# Revit family: BuzziWrap Desk
name_source: partatom
category: Furniture
revit_build: Autodesk Revit 2015 (Build: 20141119_0715(x64)
units: mm (PartAtom-declared; Revit-internal decimal feet)

## types (17) — shared parameters
BuzziWrap Desk Right Terminate 20.67x 26.18 = No
Middle Panel Length = 3' - 0"
Panel Material = <By Category>

## per-type parameters (varying)
- BuzziWrap Desk Full- 28.54 x 26.18: BuzziWrap Desk Center 20.67x 18.31=No; BuzziWrap Desk Center 20.67x 26.18=No; BuzziWrap Desk Center 24.61x 18.31=No; BuzziWrap Desk Center 24.61x 26.18=No; BuzziWrap Desk Center 28.54x 18.31=No; BuzziWrap Desk Center 28.54x 26.18=Yes; BuzziWrap Desk Left 20.67x 18.31=No; BuzziWrap Desk Left 20.67x 26.18=No; BuzziWrap Desk Left 24.61x 18.31=No; BuzziWrap Desk Left 24.61x 26.18=No; BuzziWrap Desk Left 28.54x 18.31=No; BuzziWrap Desk Left 28.54x 26.18=No; BuzziWrap Desk Left Terminate 20.67x 18.31=No; BuzziWrap Desk Left Terminate 20.67x 26.18=No; BuzziWrap Desk Left Terminate 24.61x 18.31=No; BuzziWrap Desk Left Terminate 24.61x 26.18=No; BuzziWrap Desk Left Terminate 28.54x 18.31=No; BuzziWrap Desk Left Terminate 28.54x 26.18=Yes; BuzziWrap Desk Right 20.67x 18.31=No; BuzziWrap Desk Right 20.67x 26.18=No; BuzziWrap Desk Right 24.61x 18.31=No; BuzziWrap Desk Right 24.61x 26.18=No; BuzziWrap Desk Right 28.54x 18.31=No; BuzziWrap Desk Right 28.54x 26.18=Yes; BuzziWrap Desk Right Terminate 20.67x 18.31=No; BuzziWrap Desk Right Terminate 24.61x 18.31=No; BuzziWrap Desk Right Terminate 24.61x 26.18=No; BuzziWrap Desk Right Terminate 28.54x 18.31=No; BuzziWrap Desk Right Terminate 28.54x 26.18=No
- BuzziWrap Desk Left- 28.54 x 26.18: BuzziWrap Desk Center 20.67x 18.31=No; BuzziWrap Desk Center 20.67x 26.18=No; BuzziWrap Desk Center 24.61x 18.31=No; BuzziWrap Desk Center 24.61x 26.18=No; BuzziWrap Desk Center 28.54x 18.31=No; BuzziWrap Desk Center 28.54x 26.18=Yes; BuzziWrap Desk Left 20.67x 18.31=No; BuzziWrap Desk Left 20.67x 26.18=No; BuzziWrap Desk Left 24.61x 18.31=No; BuzziWrap Desk Left 24.61x 26.18=No; BuzziWrap Desk Left 28.54x 18.31=No; BuzziWrap Desk Left 28.54x 26.18=Yes; BuzziWrap Desk Left Terminate 20.67x 18.31=No; BuzziWrap Desk Left Terminate 20.67x 26.18=No; BuzziWrap Desk Left Terminate 24.61x 18.31=No; BuzziWrap Desk Left Terminate 24.61x 26.18=No; BuzziWrap Desk Left Terminate 28.54x 18.31=No; BuzziWrap Desk Left Terminate 28.54x 26.18=No; BuzziWrap Desk Right 20.67x 18.31=No; BuzziWrap Desk Right 20.67x 26.18=No; BuzziWrap Desk Right 24.61x 18.31=No; BuzziWrap Desk Right 24.61x 26.18=No; BuzziWrap Desk Right 28.54x 18.31=No; BuzziWrap Desk Right 28.54x 26.18=No; BuzziWrap Desk Right Terminate 20.67x 18.31=No; BuzziWrap Desk Right Terminate 24.61x 18.31=No; BuzziWrap Desk Right Terminate 24.61x 26.18=No; BuzziWrap Desk Right Terminate 28.54x 18.31=No; BuzziWrap Desk Right Terminate 28.54x 26.18=Yes
- BuzziWrap Desk Right- 28.54 x 26.18: BuzziWrap Desk Center 20.67x 18.31=No; BuzziWrap Desk Center 20.67x 26.18=No; BuzziWrap Desk Center 24.61x 18.31=No; BuzziWrap Desk Center 24.61x 26.18=No; BuzziWrap Desk Center 28.54x 18.31=No; BuzziWrap Desk Center 28.54x 26.18=Yes; BuzziWrap Desk Left 20.67x 18.31=No; BuzziWrap Desk Left 20.67x 26.18=No; BuzziWrap Desk Left 24.61x 18.31=No; BuzziWrap Desk Left 24.61x 26.18=No; BuzziWrap Desk Left 28.54x 18.31=No; BuzziWrap Desk Left 28.54x 26.18=No; BuzziWrap Desk Left Terminate 20.67x 18.31=No; BuzziWrap Desk Left Terminate 20.67x 26.18=No; BuzziWrap Desk Left Terminate 24.61x 18.31=No; BuzziWrap Desk Left Terminate 24.61x 26.18=No; BuzziWrap Desk Left Terminate 28.54x 18.31=No; BuzziWrap Desk Left Terminate 28.54x 26.18=Yes; BuzziWrap Desk Right 20.67x 18.31=No; BuzziWrap Desk Right 20.67x 26.18=No; BuzziWrap Desk Right 24.61x 18.31=No; BuzziWrap Desk Right 24.61x 26.18=No; BuzziWrap Desk Right 28.54x 18.31=No; BuzziWrap Desk Right 28.54x 26.18=Yes; BuzziWrap Desk Right Terminate 20.67x 18.31=No; BuzziWrap Desk Right Terminate 24.61x 18.31=No; BuzziWrap Desk Right Terminate 24.61x 26.18=No; BuzziWrap Desk Right Terminate 28.54x 18.31=No; BuzziWrap Desk Right Terminate 28.54x 26.18=No
- BuzziWrap Desk Full- 28.54 x 18.31: BuzziWrap Desk Center 20.67x 18.31=No; BuzziWrap Desk Center 20.67x 26.18=No; BuzziWrap Desk Center 24.61x 18.31=No; BuzziWrap Desk Center 24.61x 26.18=No; BuzziWrap Desk Center 28.54x 18.31=Yes; BuzziWrap Desk Center 28.54x 26.18=No; BuzziWrap Desk Left 20.67x 18.31=No; BuzziWrap Desk Left 20.67x 26.18=No; BuzziWrap Desk Left 24.61x 18.31=No; BuzziWrap Desk Left 24.61x 26.18=No; BuzziWrap Desk Left 28.54x 18.31=Yes; BuzziWrap Desk Left 28.54x 26.18=No; BuzziWrap Desk Left Terminate 20.67x 18.31=No; BuzziWrap Desk Left Terminate 20.67x 26.18=No; BuzziWrap Desk Left Terminate 24.61x 18.31=No; BuzziWrap Desk Left Terminate 24.61x 26.18=No; BuzziWrap Desk Left Terminate 28.54x 18.31=No; BuzziWrap Desk Left Terminate 28.54x 26.18=No; BuzziWrap Desk Right 20.67x 18.31=No; BuzziWrap Desk Right 20.67x 26.18=No; BuzziWrap Desk Right 24.61x 18.31=No; BuzziWrap Desk Right 24.61x 26.18=No; BuzziWrap Desk Right 28.54x 18.31=Yes; BuzziWrap Desk Right 28.54x 26.18=No; BuzziWrap Desk Right Terminate 20.67x 18.31=No; BuzziWrap Desk Right Terminate 24.61x 18.31=No; BuzziWrap Desk Right Terminate 24.61x 26.18=No; BuzziWrap Desk Right Terminate 28.54x 18.31=No; BuzziWrap Desk Right Terminate 28.54x 26.18=No
- BuzziWrap Desk Left- 28.54 x 18.31: BuzziWrap Desk Center 20.67x 18.31=No; BuzziWrap Desk Center 20.67x 26.18=No; BuzziWrap Desk Center 24.61x 18.31=No; BuzziWrap Desk Center 24.61x 26.18=No; BuzziWrap Desk Center 28.54x 18.31=Yes; BuzziWrap Desk Center 28.54x 26.18=No; BuzziWrap Desk Left 20.67x 18.31=No; BuzziWrap Desk Left 20.67x 26.18=No; BuzziWrap Desk Left 24.61x 18.31=No; BuzziWrap Desk Left 24.61x 26.18=No; BuzziWrap Desk Left 28.54x 18.31=Yes; BuzziWrap Desk Left 28.54x 26.18=No; BuzziWrap Desk Left Terminate 20.67x 18.31=No; BuzziWrap Desk Left Terminate 20.67x 26.18=No; BuzziWrap Desk Left Terminate 24.61x 18.31=No; BuzziWrap Desk Left Terminate 24.61x 26.18=No; BuzziWrap Desk Left Terminate 28.54x 18.31=No; BuzziWrap Desk Left Terminate 28.54x 26.18=No; BuzziWrap Desk Right 20.67x 18.31=No; BuzziWrap Desk Right 20.67x 26.18=No; BuzziWrap Desk Right 24.61x 18.31=No; BuzziWrap Desk Right 24.61x 26.18=No; BuzziWrap Desk Right 28.54x 18.31=No; BuzziWrap Desk Right 28.54x 26.18=No; BuzziWrap Desk Right Terminate 20.67x 18.31=No; BuzziWrap Desk Right Terminate 24.61x 18.31=No; BuzziWrap Desk Right Terminate 24.61x 26.18=No; BuzziWrap Desk Right Terminate 28.54x 18.31=Yes; BuzziWrap Desk Right Terminate 28.54x 26.18=No
- BuzziWrap Desk Right- 28.54 x 18.31: BuzziWrap Desk Center 20.67x 18.31=No; BuzziWrap Desk Center 20.67x 26.18=No; BuzziWrap Desk Center 24.61x 18.31=No; BuzziWrap Desk Center 24.61x 26.18=No; BuzziWrap Desk Center 28.54x 18.31=Yes; BuzziWrap Desk Center 28.54x 26.18=No; BuzziWrap Desk Left 20.67x 18.31=No; BuzziWrap Desk Left 20.67x 26.18=No; BuzziWrap Desk Left 24.61x 18.31=No; BuzziWrap Desk Left 24.61x 26.18=No; BuzziWrap Desk Left 28.54x 18.31=No; BuzziWrap Desk Left 28.54x 26.18=No; BuzziWrap Desk Left Terminate 20.67x 18.31=No; BuzziWrap Desk Left Terminate 20.67x 26.18=No; BuzziWrap Desk Left Terminate 24.61x 18.31=No; BuzziWrap Desk Left Terminate 24.61x 26.18=No; BuzziWrap Desk Left Terminate 28.54x 18.31=Yes; BuzziWrap Desk Left Terminate 28.54x 26.18=No; BuzziWrap Desk Right 20.67x 18.31=No; BuzziWrap Desk Right 20.67x 26.18=No; BuzziWrap Desk Right 24.61x 18.31=No; BuzziWrap Desk Right 24.61x 26.18=No; BuzziWrap Desk Right 28.54x 18.31=Yes; BuzziWrap Desk Right 28.54x 26.18=No; BuzziWrap Desk Right Terminate 20.67x 18.31=No; BuzziWrap Desk Right Terminate 24.61x 18.31=No; BuzziWrap Desk Right Terminate 24.61x 26.18=No; BuzziWrap Desk Right Terminate 28.54x 18.31=No; BuzziWrap Desk Right Terminate 28.54x 26.18=No
- BuzziWrap desk Full- 24.61 x 26.18: BuzziWrap Desk Center 20.67x 18.31=No; BuzziWrap Desk Center 20.67x 26.18=No; BuzziWrap Desk Center 24.61x 18.31=No; BuzziWrap Desk Center 24.61x 26.18=Yes; BuzziWrap Desk Center 28.54x 18.31=No; BuzziWrap Desk Center 28.54x 26.18=No; BuzziWrap Desk Left 20.67x 18.31=No; BuzziWrap Desk Left 20.67x 26.18=No; BuzziWrap Desk Left 24.61x 18.31=No; BuzziWrap Desk Left 24.61x 26.18=Yes; BuzziWrap Desk Left 28.54x 18.31=No; BuzziWrap Desk Left 28.54x 26.18=No; BuzziWrap Desk Left Terminate 20.67x 18.31=No; BuzziWrap Desk Left Terminate 20.67x 26.18=No; BuzziWrap Desk Left Terminate 24.61x 18.31=No; BuzziWrap Desk Left Terminate 24.61x 26.18=No; BuzziWrap Desk Left Terminate 28.54x 18.31=No; BuzziWrap Desk Left Terminate 28.54x 26.18=No; BuzziWrap Desk Right 20.67x 18.31=No; BuzziWrap Desk Right 20.67x 26.18=No; BuzziWrap Desk Right 24.61x 18.31=No; BuzziWrap Desk Right 24.61x 26.18=Yes; BuzziWrap Desk Right 28.54x 18.31=No; BuzziWrap Desk Right 28.54x 26.18=No; BuzziWrap Desk Right Terminate 20.67x 18.31=No; BuzziWrap Desk Right Terminate 24.61x 18.31=No; BuzziWrap Desk Right Terminate 24.61x 26.18=No; BuzziWrap Desk Right Terminate 28.54x 18.31=No; BuzziWrap Desk Right Terminate 28.54x 26.18=No
- BuzziWrap desk Left- 24.61 x 26.18: BuzziWrap Desk Center 20.67x 18.31=No; BuzziWrap Desk Center 20.67x 26.18=No; BuzziWrap Desk Center 24.61x 18.31=Yes; BuzziWrap Desk Center 24.61x 26.18=Yes; BuzziWrap Desk Center 28.54x 18.31=No; BuzziWrap Desk Center 28.54x 26.18=No; BuzziWrap Desk Left 20.67x 18.31=No; BuzziWrap Desk Left 20.67x 26.18=No; BuzziWrap Desk Left 24.61x 18.31=No; BuzziWrap Desk Left 24.61x 26.18=Yes; BuzziWrap Desk Left 28.54x 18.31=No; BuzziWrap Desk Left 28.54x 26.18=No; BuzziWrap Desk Left Terminate 20.67x 18.31=Yes; BuzziWrap Desk Left Terminate 20.67x 26.18=No; BuzziWrap Desk Left Terminate 24.61x 18.31=Yes; BuzziWrap Desk Left Terminate 24.61x 26.18=No; BuzziWrap Desk Left Terminate 28.54x 18.31=No; BuzziWrap Desk Left Terminate 28.54x 26.18=No; BuzziWrap Desk Right 20.67x 18.31=No; BuzziWrap Desk Right 20.67x 26.18=No; BuzziWrap Desk Right 24.61x 18.31=No; BuzziWrap Desk Right 24.61x 26.18=No; BuzziWrap Desk Right 28.54x 18.31=No; BuzziWrap Desk Right 28.54x 26.18=No; BuzziWrap Desk Right Terminate 20.67x 18.31=Yes; BuzziWrap Desk Right Terminate 24.61x 18.31=Yes; BuzziWrap Desk Right Terminate 24.61x 26.18=Yes; BuzziWrap Desk Right Terminate 28.54x 18.31=No; BuzziWrap Desk Right Terminate 28.54x 26.18=No
- BuzziWrap Desk Right 24.61 x 26.18: BuzziWrap Desk Center 20.67x 18.31=No; BuzziWrap Desk Center 20.67x 26.18=No; BuzziWrap Desk Center 24.61x 18.31=No; BuzziWrap Desk Center 24.61x 26.18=Yes; BuzziWrap Desk Center 28.54x 18.31=No; BuzziWrap Desk Center 28.54x 26.18=No; BuzziWrap Desk Left 20.67x 18.31=No; BuzziWrap Desk Left 20.67x 26.18=No; BuzziWrap Desk Left 24.61x 18.31=No; BuzziWrap Desk Left 24.61x 26.18=No; BuzziWrap Desk Left 28.54x 18.31=No; BuzziWrap Desk Left 28.54x 26.18=No; BuzziWrap Desk Left Terminate 20.67x 18.31=No; BuzziWrap Desk Left Terminate 20.67x 26.18=No; BuzziWrap Desk Left Terminate 24.61x 18.31=No; BuzziWrap Desk Left Terminate 24.61x 26.18=Yes; BuzziWrap Desk Left Terminate 28.54x 18.31=No; BuzziWrap Desk Left Terminate 28.54x 26.18=No; BuzziWrap Desk Right 20.67x 18.31=No; BuzziWrap Desk Right 20.67x 26.18=No; BuzziWrap Desk Right 24.61x 18.31=No; BuzziWrap Desk Right 24.61x 26.18=Yes; BuzziWrap Desk Right 28.54x 18.31=No; BuzziWrap Desk Right 28.54x 26.18=No; BuzziWrap Desk Right Terminate 20.67x 18.31=No; BuzziWrap Desk Right Terminate 24.61x 18.31=No; BuzziWrap Desk Right Terminate 24.61x 26.18=No; BuzziWrap Desk Right Terminate 28.54x 18.31=No; BuzziWrap Desk Right Terminate 28.54x 26.18=No
- BuzziWrap Desk Full 24.61 x 18.31: BuzziWrap Desk Center 20.67x 18.31=No; BuzziWrap Desk Center 20.67x 26.18=No; BuzziWrap Desk Center 24.61x 18.31=Yes; BuzziWrap Desk Center 24.61x 26.18=No; BuzziWrap Desk Center 28.54x 18.31=No; BuzziWrap Desk Center 28.54x 26.18=No; BuzziWrap Desk Left 20.67x 18.31=No; BuzziWrap Desk Left 20.67x 26.18=No; BuzziWrap Desk Left 24.61x 18.31=Yes; BuzziWrap Desk Left 24.61x 26.18=No; BuzziWrap Desk Left 28.54x 18.31=No; BuzziWrap Desk Left 28.54x 26.18=No; BuzziWrap Desk Left Terminate 20.67x 18.31=No; BuzziWrap Desk Left Terminate 20.67x 26.18=No; BuzziWrap Desk Left Terminate 24.61x 18.31=No; BuzziWrap Desk Left Terminate 24.61x 26.18=No; BuzziWrap Desk Left Terminate 28.54x 18.31=No; BuzziWrap Desk Left Terminate 28.54x 26.18=No; BuzziWrap Desk Right 20.67x 18.31=No; BuzziWrap Desk Right 20.67x 26.18=No; BuzziWrap Desk Right 24.61x 18.31=Yes; BuzziWrap Desk Right 24.61x 26.18=No; BuzziWrap Desk Right 28.54x 18.31=No; BuzziWrap Desk Right 28.54x 26.18=No; BuzziWrap Desk Right Terminate 20.67x 18.31=No; BuzziWrap Desk Right Terminate 24.61x 18.31=No; BuzziWrap Desk Right Terminate 24.61x 26.18=No; BuzziWrap Desk Right Terminate 28.54x 18.31=No; BuzziWrap Desk Right Terminate 28.54x 26.18=No
- BuzziWrap Desk Left 24.61 x 18.31: BuzziWrap Desk Center 20.67x 18.31=No; BuzziWrap Desk Center 20.67x 26.18=No; BuzziWrap Desk Center 24.61x 18.31=Yes; BuzziWrap Desk Center 24.61x 26.18=No; BuzziWrap Desk Center 28.54x 18.31=No; BuzziWrap Desk Center 28.54x 26.18=No; BuzziWrap Desk Left 20.67x 18.31=No; BuzziWrap Desk Left 20.67x 26.18=No; BuzziWrap Desk Left 24.61x 18.31=Yes; BuzziWrap Desk Left 24.61x 26.18=No; BuzziWrap Desk Left 28.54x 18.31=No; BuzziWrap Desk Left 28.54x 26.18=No; BuzziWrap Desk Left Terminate 20.67x 18.31=No; BuzziWrap Desk Left Terminate 20.67x 26.18=No; BuzziWrap Desk Left Terminate 24.61x 18.31=No; BuzziWrap Desk Left Terminate 24.61x 26.18=No; BuzziWrap Desk Left Terminate 28.54x 18.31=No; BuzziWrap Desk Left Terminate 28.54x 26.18=No; BuzziWrap Desk Right 20.67x 18.31=No; BuzziWrap Desk Right 20.67x 26.18=No; BuzziWrap Desk Right 24.61x 18.31=No; BuzziWrap Desk Right 24.61x 26.18=No; BuzziWrap Desk Right 28.54x 18.31=No; BuzziWrap Desk Right 28.54x 26.18=No; BuzziWrap Desk Right Terminate 20.67x 18.31=No; BuzziWrap Desk Right Terminate 24.61x 18.31=Yes; BuzziWrap Desk Right Terminate 24.61x 26.18=No; BuzziWrap Desk Right Terminate 28.54x 18.31=No; BuzziWrap Desk Right Terminate 28.54x 26.18=No
- BuzziWrap Desk Right 24.61 x 18.31: BuzziWrap Desk Center 20.67x 18.31=No; BuzziWrap Desk Center 20.67x 26.18=No; BuzziWrap Desk Center 24.61x 18.31=Yes; BuzziWrap Desk Center 24.61x 26.18=No; BuzziWrap Desk Center 28.54x 18.31=No; BuzziWrap Desk Center 28.54x 26.18=No; BuzziWrap Desk Left 20.67x 18.31=No; BuzziWrap Desk Left 20.67x 26.18=No; BuzziWrap Desk Left 24.61x 18.31=No; BuzziWrap Desk Left 24.61x 26.18=No; BuzziWrap Desk Left 28.54x 18.31=No; BuzziWrap Desk Left 28.54x 26.18=No; BuzziWrap Desk Left Terminate 20.67x 18.31=No; BuzziWrap Desk Left Terminate 20.67x 26.18=No; BuzziWrap Desk Left Terminate 24.61x 18.31=Yes; BuzziWrap Desk Left Terminate 24.61x 26.18=No; BuzziWrap Desk Left Terminate 28.54x 18.31=No; BuzziWrap Desk Left Terminate 28.54x 26.18=No; BuzziWrap Desk Right 20.67x 18.31=No; BuzziWrap Desk Right 20.67x 26.18=No; BuzziWrap Desk Right 24.61x 18.31=Yes; BuzziWrap Desk Right 24.61x 26.18=No; BuzziWrap Desk Right 28.54x 18.31=No; BuzziWrap Desk Right 28.54x 26.18=No; BuzziWrap Desk Right Terminate 20.67x 18.31=No; BuzziWrap Desk Right Terminate 24.61x 18.31=No; BuzziWrap Desk Right Terminate 24.61x 26.18=No; BuzziWrap Desk Right Terminate 28.54x 18.31=No; BuzziWrap Desk Right Terminate 28.54x 26.18=No
- BuzziWrap Desk Full 20.67 x 26.18: BuzziWrap Desk Center 20.67x 18.31=No; BuzziWrap Desk Center 20.67x 26.18=Yes; BuzziWrap Desk Center 24.61x 18.31=No; BuzziWrap Desk Center 24.61x 26.18=No; BuzziWrap Desk Center 28.54x 18.31=No; BuzziWrap Desk Center 28.54x 26.18=No; BuzziWrap Desk Left 20.67x 18.31=No; BuzziWrap Desk Left 20.67x 26.18=Yes; BuzziWrap Desk Left 24.61x 18.31=No; BuzziWrap Desk Left 24.61x 26.18=No; BuzziWrap Desk Left 28.54x 18.31=No; BuzziWrap Desk Left 28.54x 26.18=No; BuzziWrap Desk Left Terminate 20.67x 18.31=No; BuzziWrap Desk Left Terminate 20.67x 26.18=No; BuzziWrap Desk Left Terminate 24.61x 18.31=No; BuzziWrap Desk Left Terminate 24.61x 26.18=No; BuzziWrap Desk Left Terminate 28.54x 18.31=No; BuzziWrap Desk Left Terminate 28.54x 26.18=No; BuzziWrap Desk Right 20.67x 18.31=No; BuzziWrap Desk Right 20.67x 26.18=Yes; BuzziWrap Desk Right 24.61x 18.31=No; BuzziWrap Desk Right 24.61x 26.18=No; BuzziWrap Desk Right 28.54x 18.31=No; BuzziWrap Desk Right 28.54x 26.18=No; BuzziWrap Desk Right Terminate 20.67x 18.31=No; BuzziWrap Desk Right Terminate 24.61x 18.31=No; BuzziWrap Desk Right Terminate 24.61x 26.18=No; BuzziWrap Desk Right Terminate 28.54x 18.31=No; BuzziWrap Desk Right Terminate 28.54x 26.18=No
- BuzziWrap Desk Right 20.67 x 26.18: BuzziWrap Desk Center 20.67x 18.31=No; BuzziWrap Desk Center 20.67x 26.18=Yes; BuzziWrap Desk Center 24.61x 18.31=No; BuzziWrap Desk Center 24.61x 26.18=No; BuzziWrap Desk Center 28.54x 18.31=No; BuzziWrap Desk Center 28.54x 26.18=No; BuzziWrap Desk Left 20.67x 18.31=No; BuzziWrap Desk Left 20.67x 26.18=No; BuzziWrap Desk Left 24.61x 18.31=No; BuzziWrap Desk Left 24.61x 26.18=No; BuzziWrap Desk Left 28.54x 18.31=No; BuzziWrap Desk Left 28.54x 26.18=No; BuzziWrap Desk Left Terminate 20.67x 18.31=No; BuzziWrap Desk Left Terminate 20.67x 26.18=Yes; BuzziWrap Desk Left Terminate 24.61x 18.31=No; BuzziWrap Desk Left Terminate 24.61x 26.18=No; BuzziWrap Desk Left Terminate 28.54x 18.31=No; BuzziWrap Desk Left Terminate 28.54x 26.18=No; BuzziWrap Desk Right 20.67x 18.31=No; BuzziWrap Desk Right 20.67x 26.18=Yes; BuzziWrap Desk Right 24.61x 18.31=No; BuzziWrap Desk Right 24.61x 26.18=No; BuzziWrap Desk Right 28.54x 18.31=No; BuzziWrap Desk Right 28.54x 26.18=No; BuzziWrap Desk Right Terminate 20.67x 18.31=No; BuzziWrap Desk Right Terminate 24.61x 18.31=No; BuzziWrap Desk Right Terminate 24.61x 26.18=No; BuzziWrap Desk Right Terminate 28.54x 18.31=No; BuzziWrap Desk Right Terminate 28.54x 26.18=No
- BuzziWrap Desk Full 20.67 x 18.31: BuzziWrap Desk Center 20.67x 18.31=Yes; BuzziWrap Desk Center 20.67x 26.18=No; BuzziWrap Desk Center 24.61x 18.31=No; BuzziWrap Desk Center 24.61x 26.18=No; BuzziWrap Desk Center 28.54x 18.31=No; BuzziWrap Desk Center 28.54x 26.18=No; BuzziWrap Desk Left 20.67x 18.31=Yes; BuzziWrap Desk Left 20.67x 26.18=No; BuzziWrap Desk Left 24.61x 18.31=No; BuzziWrap Desk Left 24.61x 26.18=No; BuzziWrap Desk Left 28.54x 18.31=No; BuzziWrap Desk Left 28.54x 26.18=No; BuzziWrap Desk Left Terminate 20.67x 18.31=No; BuzziWrap Desk Left Terminate 20.67x 26.18=No; BuzziWrap Desk Left Terminate 24.61x 18.31=No; BuzziWrap Desk Left Terminate 24.61x 26.18=No; BuzziWrap Desk Left Terminate 28.54x 18.31=No; BuzziWrap Desk Left Terminate 28.54x 26.18=No; BuzziWrap Desk Right 20.67x 18.31=Yes; BuzziWrap Desk Right 20.67x 26.18=No; BuzziWrap Desk Right 24.61x 18.31=No; BuzziWrap Desk Right 24.61x 26.18=No; BuzziWrap Desk Right 28.54x 18.31=No; BuzziWrap Desk Right 28.54x 26.18=No; BuzziWrap Desk Right Terminate 20.67x 18.31=No; BuzziWrap Desk Right Terminate 24.61x 18.31=No; BuzziWrap Desk Right Terminate 24.61x 26.18=No; BuzziWrap Desk Right Terminate 28.54x 18.31=No; BuzziWrap Desk Right Terminate 28.54x 26.18=No
- BuzziWrap Desk Left 20.67 x 18.31: BuzziWrap Desk Center 20.67x 18.31=Yes; BuzziWrap Desk Center 20.67x 26.18=No; BuzziWrap Desk Center 24.61x 18.31=No; BuzziWrap Desk Center 24.61x 26.18=No; BuzziWrap Desk Center 28.54x 18.31=No; BuzziWrap Desk Center 28.54x 26.18=No; BuzziWrap Desk Left 20.67x 18.31=Yes; BuzziWrap Desk Left 20.67x 26.18=No; BuzziWrap Desk Left 24.61x 18.31=No; BuzziWrap Desk Left 24.61x 26.18=No; BuzziWrap Desk Left 28.54x 18.31=No; BuzziWrap Desk Left 28.54x 26.18=No; BuzziWrap Desk Left Terminate 20.67x 18.31=No; BuzziWrap Desk Left Terminate 20.67x 26.18=No; BuzziWrap Desk Left Terminate 24.61x 18.31=No; BuzziWrap Desk Left Terminate 24.61x 26.18=No; BuzziWrap Desk Left Terminate 28.54x 18.31=No; BuzziWrap Desk Left Terminate 28.54x 26.18=No; BuzziWrap Desk Right 20.67x 18.31=No; BuzziWrap Desk Right 20.67x 26.18=No; BuzziWrap Desk Right 24.61x 18.31=No; BuzziWrap Desk Right 24.61x 26.18=No; BuzziWrap Desk Right 28.54x 18.31=No; BuzziWrap Desk Right 28.54x 26.18=No; BuzziWrap Desk Right Terminate 20.67x 18.31=Yes; BuzziWrap Desk Right Terminate 24.61x 18.31=No; BuzziWrap Desk Right Terminate 24.61x 26.18=No; BuzziWrap Desk Right Terminate 28.54x 18.31=No; BuzziWrap Desk Right Terminate 28.54x 26.18=No
- BuzziWrap Desk Right 20.67 x 18.31: BuzziWrap Desk Center 20.67x 18.31=Yes; BuzziWrap Desk Center 20.67x 26.18=No; BuzziWrap Desk Center 24.61x 18.31=No; BuzziWrap Desk Center 24.61x 26.18=No; BuzziWrap Desk Center 28.54x 18.31=No; BuzziWrap Desk Center 28.54x 26.18=No; BuzziWrap Desk Left 20.67x 18.31=No; BuzziWrap Desk Left 20.67x 26.18=No; BuzziWrap Desk Left 24.61x 18.31=No; BuzziWrap Desk Left 24.61x 26.18=No; BuzziWrap Desk Left 28.54x 18.31=No; BuzziWrap Desk Left 28.54x 26.18=No; BuzziWrap Desk Left Terminate 20.67x 18.31=Yes; BuzziWrap Desk Left Terminate 20.67x 26.18=No; BuzziWrap Desk Left Terminate 24.61x 18.31=No; BuzziWrap Desk Left Terminate 24.61x 26.18=No; BuzziWrap Desk Left Terminate 28.54x 18.31=No; BuzziWrap Desk Left Terminate 28.54x 26.18=No; BuzziWrap Desk Right 20.67x 18.31=Yes; BuzziWrap Desk Right 20.67x 26.18=No; BuzziWrap Desk Right 24.61x 18.31=No; BuzziWrap Desk Right 24.61x 26.18=No; BuzziWrap Desk Right 28.54x 18.31=No; BuzziWrap Desk Right 28.54x 26.18=No; BuzziWrap Desk Right Terminate 20.67x 18.31=No; BuzziWrap Desk Right Terminate 24.61x 18.31=No; BuzziWrap Desk Right Terminate 24.61x 26.18=No; BuzziWrap Desk Right Terminate 28.54x 18.31=No; BuzziWrap Desk Right Terminate 28.54x 26.18=No

## geometry (parser evidence)
native form markers: Sweep x47
no freeform markers — native parametric forms only
